# Revit family: Gira_2832005
name_source: partatom
category: Electrical Fixtures
revit_build: Autodesk Revit 2017 (Build: 20160225_1515(x64)
units: mm (PartAtom-declared; Revit-internal decimal feet)

## family parameters
Cut with Voids When Loaded = No
Host = Face
Maintain Annotation Orientation = Yes
Part Type = Normal
Room Calculation Point = No
Round Connector Dimension = Use Diameter
Shared = No

## types (1)
- Rocker sw. BS 3-g off/2-way System 55 black m
    Available = No
    BIM (1) = https://media.stage.bim.site und Tasten.rfa?public/gira/36a6b08/Sys55_Komplettgerät_Schalten und Tasten.rfa
    Category = Switch
    Data sheet (1) = https://katalog.gira.de
    Default Elevation = 1219 mm
    Description = Rock.sw.3g 2-w Sys55 BKm,British Standard rocker switch (BS EN 60669-1) 3-gang with rockers,System 55, Support ring 71 x 71 mm, universal off 2-way switch,black matt,Features:,- With screw terminals.,,Notes :,- For screw mounting only.
    GTIN = 4010337038528
    HAN = 2832005
    HeinzeBIM = https://bimportal.heinze.de
    Label space/information surface = No
    Manufacturer = Gira
    Manufacturer URL = https://www.gira.de
    Model = Sys55_Komplettgerät_Schalten und Tasten
    Name = Rocker sw. BS 3-g off/2-way System 55 black m
    URL = http://katalog.gira.de

## geometry (parser evidence)
native form markers: Blend x2, Sweep x6
no freeform markers — native parametric forms only
